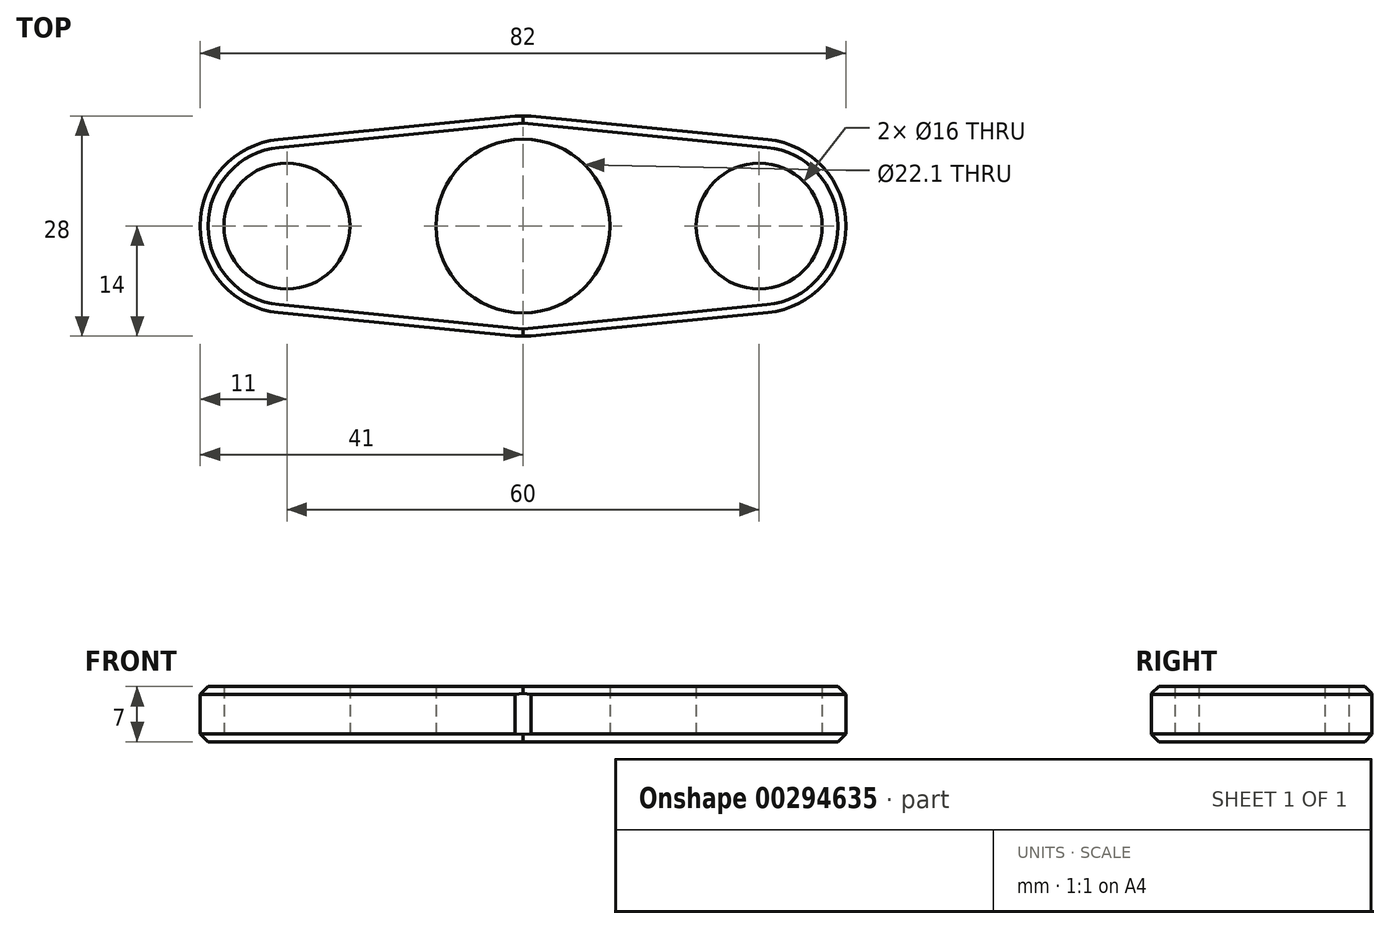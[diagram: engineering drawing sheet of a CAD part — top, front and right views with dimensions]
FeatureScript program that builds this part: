
annotation { "Feature Type Name" : "Feature", "Feature Type Description" : "" }
export const myFeature = defineFeature(function(context is Context, id is Id, definition is map)
    precondition{}
    {
        {
            var Q0;
            Q0=qCreatedBy(makeId("Top.planeOp"),FACE);
            var sketch = newSketch(context, id + "F0", { "sketchPlane" : qUnion([Q0])});
            skLineSegment(sketch, "E0.bottom", {"start": v(41, 14) * mm, "end": v(-41, 14) * mm});
            skLineSegment(sketch, "E0.top", {"start": v(41, -14) * mm, "end": v(-41, -14) * mm});
            skLineSegment(sketch, "E0.left", {"start": v(41, 14) * mm, "end": v(41, -14) * mm});
            skLineSegment(sketch, "E0.right", {"start": v(-41, 14) * mm, "end": v(-41, -14) * mm});
            skPoint(sketch, "E0.middle", {"position": v(0, 0) * mm});
            skCircle(sketch, "E1", {"center": v(0, 0) * mm, "radius": 11.05 * mm});
            skCircle(sketch, "E2", {"center": v(-30, 0) * mm, "radius": 8 * mm});
            skCircle(sketch, "E3", {"center": v(30, 0) * mm, "radius": 8 * mm});
            skSolve(sketch);
        }
        {
            var Q0;
            Q0=makeQuery(id+"F0.imprint","IMPRINT",FACE,{"disambiguationData":[TD([[makeQuery(id+"F0.imprint","IMPRINT",EDGE,{"derivedFrom":sQuery(id+"F0.wireOp",EDGE,"E0.bottom")}),1.0]])]});
            extrude(context, id + "F1", {"entities" : qUnion([Q0]), "depth" : 7 * mm});
        }
        {
            var Q0;
            Q0=makeQuery(id+"F1.opExtrude","SWEPT_EDGE",EDGE,{"disambiguationData":[OSD([sQuery(id+"F0.wireOp",EDGE,"E0.top"),sQuery(id+"F0.wireOp",EDGE,"E0.right")])]});
            var Q1;
            Q1=makeQuery(id+"F1.opExtrude","SWEPT_EDGE",EDGE,{"disambiguationData":[OSD([sQuery(id+"F0.wireOp",EDGE,"E0.top"),sQuery(id+"F0.wireOp",EDGE,"E0.left")])]});
            var Q2;
            Q2=makeQuery(id+"F1.opExtrude","SWEPT_EDGE",EDGE,{"disambiguationData":[OSD([sQuery(id+"F0.wireOp",EDGE,"E0.bottom"),sQuery(id+"F0.wireOp",EDGE,"E0.left")])]});
            var Q3;
            Q3=makeQuery(id+"F1.opExtrude","SWEPT_EDGE",EDGE,{"disambiguationData":[OSD([sQuery(id+"F0.wireOp",EDGE,"E0.bottom"),sQuery(id+"F0.wireOp",EDGE,"E0.right")])]});
            chamfer(context, id + "F2", {"entities" : qUnion([Q0, Q1, Q2, Q3]), "chamferType" : ChamferType.TWO_OFFSETS, "width1" : 40 * mm, "oppositeDirection" : false, "width2" : 4 * mm, "tangentPropagation" : true});
        }
        {
            var Q0;
            {var subQ0=sQuery(id+"F0.wireOp",EDGE,"E0.right");Q0=makeQuery(id+"F2.opChamfer","BLEND_EDGE",EDGE,{"blendedFrom":[makeQuery(id+"F1.opExtrude","SWEPT_EDGE",EDGE,{"disambiguationData":[OSD([sQuery(id+"F0.wireOp",EDGE,"E0.bottom"),subQ0])]}),makeQuery(id+"F1.opExtrude","SWEPT_FACE",FACE,{"disambiguationData":[OSD([subQ0])]})],"blendedInto":[makeQuery(id+"F1.opExtrude","SWEPT_FACE",FACE,{"disambiguationData":[OSD([subQ0])]})]});}
            var Q1;
            {var subQ0=sQuery(id+"F0.wireOp",EDGE,"E0.right");Q1=makeQuery(id+"F2.opChamfer","BLEND_EDGE",EDGE,{"blendedFrom":[makeQuery(id+"F1.opExtrude","SWEPT_EDGE",EDGE,{"disambiguationData":[OSD([sQuery(id+"F0.wireOp",EDGE,"E0.top"),subQ0])]}),makeQuery(id+"F1.opExtrude","SWEPT_FACE",FACE,{"disambiguationData":[OSD([subQ0])]})],"blendedInto":[makeQuery(id+"F1.opExtrude","SWEPT_FACE",FACE,{"disambiguationData":[OSD([subQ0])]})]});}
            var Q2;
            {var subQ0=sQuery(id+"F0.wireOp",EDGE,"E0.left");Q2=makeQuery(id+"F2.opChamfer","BLEND_EDGE",EDGE,{"blendedFrom":[makeQuery(id+"F1.opExtrude","SWEPT_EDGE",EDGE,{"disambiguationData":[OSD([sQuery(id+"F0.wireOp",EDGE,"E0.bottom"),subQ0])]}),makeQuery(id+"F1.opExtrude","SWEPT_FACE",FACE,{"disambiguationData":[OSD([subQ0])]})],"blendedInto":[makeQuery(id+"F1.opExtrude","SWEPT_FACE",FACE,{"disambiguationData":[OSD([subQ0])]})]});}
            var Q3;
            {var subQ0=sQuery(id+"F0.wireOp",EDGE,"E0.left");Q3=makeQuery(id+"F2.opChamfer","BLEND_EDGE",EDGE,{"blendedFrom":[makeQuery(id+"F1.opExtrude","SWEPT_EDGE",EDGE,{"disambiguationData":[OSD([sQuery(id+"F0.wireOp",EDGE,"E0.top"),subQ0])]}),makeQuery(id+"F1.opExtrude","SWEPT_FACE",FACE,{"disambiguationData":[OSD([subQ0])]})],"blendedInto":[makeQuery(id+"F1.opExtrude","SWEPT_FACE",FACE,{"disambiguationData":[OSD([subQ0])]})]});}
            fillet(context, id + "F3", {"entities" : qUnion([Q0, Q1, Q2, Q3]), "radius" : 11 * mm, "tangentPropagation" : true, "allowEdgeOverflow" : false});
        }
        {
            var Q0;
            {var subQ0=sQuery(id+"F0.wireOp",EDGE,"E0.right");var subQ1=sQuery(id+"F0.wireOp",EDGE,"E0.top");Q0=makeQuery(id+"F2.opChamfer","BLEND_EDGE",EDGE,{"blendedFrom":[makeQuery(id+"F1.opExtrude","SWEPT_EDGE",EDGE,{"disambiguationData":[OSD([subQ1,subQ0])]}),makeQuery(id+"F1.opExtrude","CAP_FACE",FACE,{"disambiguationData":[OSD([sQuery(id+"F0.wireOp",EDGE,"E0.bottom"),subQ1,sQuery(id+"F0.wireOp",EDGE,"E0.left"),subQ0,sQuery(id+"F0.wireOp",EDGE,"E1"),sQuery(id+"F0.wireOp",EDGE,"E2"),sQuery(id+"F0.wireOp",EDGE,"E3")])],"isStart":false})],"blendedInto":[makeQuery(id+"F1.opExtrude","CAP_FACE",FACE,{"disambiguationData":[OSD([sQuery(id+"F0.wireOp",EDGE,"E0.bottom"),subQ1,sQuery(id+"F0.wireOp",EDGE,"E0.left"),subQ0,sQuery(id+"F0.wireOp",EDGE,"E1"),sQuery(id+"F0.wireOp",EDGE,"E2"),sQuery(id+"F0.wireOp",EDGE,"E3")])],"isStart":false})]});}
            var Q1;
            {var subQ0=sQuery(id+"F0.wireOp",EDGE,"E0.left");var subQ1=sQuery(id+"F0.wireOp",EDGE,"E0.top");Q1=makeQuery(id+"F2.opChamfer","BLEND_EDGE",EDGE,{"blendedFrom":[makeQuery(id+"F1.opExtrude","SWEPT_EDGE",EDGE,{"disambiguationData":[OSD([subQ1,subQ0])]}),makeQuery(id+"F1.opExtrude","CAP_FACE",FACE,{"disambiguationData":[OSD([sQuery(id+"F0.wireOp",EDGE,"E0.bottom"),subQ1,subQ0,sQuery(id+"F0.wireOp",EDGE,"E0.right"),sQuery(id+"F0.wireOp",EDGE,"E1"),sQuery(id+"F0.wireOp",EDGE,"E2"),sQuery(id+"F0.wireOp",EDGE,"E3")])],"isStart":false})],"blendedInto":[makeQuery(id+"F1.opExtrude","CAP_FACE",FACE,{"disambiguationData":[OSD([sQuery(id+"F0.wireOp",EDGE,"E0.bottom"),subQ1,subQ0,sQuery(id+"F0.wireOp",EDGE,"E0.right"),sQuery(id+"F0.wireOp",EDGE,"E1"),sQuery(id+"F0.wireOp",EDGE,"E2"),sQuery(id+"F0.wireOp",EDGE,"E3")])],"isStart":false})]});}
            var Q2;
            {var subQ0=sQuery(id+"F0.wireOp",EDGE,"E0.left");var subQ1=sQuery(id+"F0.wireOp",EDGE,"E0.bottom");Q2=makeQuery(id+"F2.opChamfer","BLEND_EDGE",EDGE,{"blendedFrom":[makeQuery(id+"F1.opExtrude","SWEPT_EDGE",EDGE,{"disambiguationData":[OSD([subQ1,subQ0])]}),makeQuery(id+"F1.opExtrude","CAP_FACE",FACE,{"disambiguationData":[OSD([subQ1,sQuery(id+"F0.wireOp",EDGE,"E0.top"),subQ0,sQuery(id+"F0.wireOp",EDGE,"E0.right"),sQuery(id+"F0.wireOp",EDGE,"E1"),sQuery(id+"F0.wireOp",EDGE,"E2"),sQuery(id+"F0.wireOp",EDGE,"E3")])],"isStart":false})],"blendedInto":[makeQuery(id+"F1.opExtrude","CAP_FACE",FACE,{"disambiguationData":[OSD([subQ1,sQuery(id+"F0.wireOp",EDGE,"E0.top"),subQ0,sQuery(id+"F0.wireOp",EDGE,"E0.right"),sQuery(id+"F0.wireOp",EDGE,"E1"),sQuery(id+"F0.wireOp",EDGE,"E2"),sQuery(id+"F0.wireOp",EDGE,"E3")])],"isStart":false})]});}
            var Q3;
            {var subQ0=sQuery(id+"F0.wireOp",EDGE,"E0.right");var subQ1=sQuery(id+"F0.wireOp",EDGE,"E0.bottom");Q3=makeQuery(id+"F2.opChamfer","BLEND_EDGE",EDGE,{"blendedFrom":[makeQuery(id+"F1.opExtrude","SWEPT_EDGE",EDGE,{"disambiguationData":[OSD([subQ1,subQ0])]}),makeQuery(id+"F1.opExtrude","CAP_FACE",FACE,{"disambiguationData":[OSD([subQ1,sQuery(id+"F0.wireOp",EDGE,"E0.top"),sQuery(id+"F0.wireOp",EDGE,"E0.left"),subQ0,sQuery(id+"F0.wireOp",EDGE,"E1"),sQuery(id+"F0.wireOp",EDGE,"E2"),sQuery(id+"F0.wireOp",EDGE,"E3")])],"isStart":false})],"blendedInto":[makeQuery(id+"F1.opExtrude","CAP_FACE",FACE,{"disambiguationData":[OSD([subQ1,sQuery(id+"F0.wireOp",EDGE,"E0.top"),sQuery(id+"F0.wireOp",EDGE,"E0.left"),subQ0,sQuery(id+"F0.wireOp",EDGE,"E1"),sQuery(id+"F0.wireOp",EDGE,"E2"),sQuery(id+"F0.wireOp",EDGE,"E3")])],"isStart":false})]});}
            var Q4;
            {var subQ0=sQuery(id+"F0.wireOp",EDGE,"E0.left");var subQ1=sQuery(id+"F0.wireOp",EDGE,"E0.top");Q4=makeQuery(id+"F2.opChamfer","BLEND_EDGE",EDGE,{"blendedFrom":[makeQuery(id+"F1.opExtrude","SWEPT_EDGE",EDGE,{"disambiguationData":[OSD([subQ1,subQ0])]}),makeQuery(id+"F1.opExtrude","CAP_FACE",FACE,{"disambiguationData":[OSD([sQuery(id+"F0.wireOp",EDGE,"E0.bottom"),subQ1,subQ0,sQuery(id+"F0.wireOp",EDGE,"E0.right"),sQuery(id+"F0.wireOp",EDGE,"E1"),sQuery(id+"F0.wireOp",EDGE,"E2"),sQuery(id+"F0.wireOp",EDGE,"E3")])],"isStart":true})],"blendedInto":[makeQuery(id+"F1.opExtrude","CAP_FACE",FACE,{"disambiguationData":[OSD([sQuery(id+"F0.wireOp",EDGE,"E0.bottom"),subQ1,subQ0,sQuery(id+"F0.wireOp",EDGE,"E0.right"),sQuery(id+"F0.wireOp",EDGE,"E1"),sQuery(id+"F0.wireOp",EDGE,"E2"),sQuery(id+"F0.wireOp",EDGE,"E3")])],"isStart":true})]});}
            var Q5;
            {var subQ0=sQuery(id+"F0.wireOp",EDGE,"E0.right");var subQ1=sQuery(id+"F0.wireOp",EDGE,"E0.top");Q5=makeQuery(id+"F2.opChamfer","BLEND_EDGE",EDGE,{"blendedFrom":[makeQuery(id+"F1.opExtrude","SWEPT_EDGE",EDGE,{"disambiguationData":[OSD([subQ1,subQ0])]}),makeQuery(id+"F1.opExtrude","CAP_FACE",FACE,{"disambiguationData":[OSD([sQuery(id+"F0.wireOp",EDGE,"E0.bottom"),subQ1,sQuery(id+"F0.wireOp",EDGE,"E0.left"),subQ0,sQuery(id+"F0.wireOp",EDGE,"E1"),sQuery(id+"F0.wireOp",EDGE,"E2"),sQuery(id+"F0.wireOp",EDGE,"E3")])],"isStart":true})],"blendedInto":[makeQuery(id+"F1.opExtrude","CAP_FACE",FACE,{"disambiguationData":[OSD([sQuery(id+"F0.wireOp",EDGE,"E0.bottom"),subQ1,sQuery(id+"F0.wireOp",EDGE,"E0.left"),subQ0,sQuery(id+"F0.wireOp",EDGE,"E1"),sQuery(id+"F0.wireOp",EDGE,"E2"),sQuery(id+"F0.wireOp",EDGE,"E3")])],"isStart":true})]});}
            var Q6;
            {var subQ0=sQuery(id+"F0.wireOp",EDGE,"E0.left");var subQ1=sQuery(id+"F0.wireOp",EDGE,"E0.bottom");Q6=makeQuery(id+"F2.opChamfer","BLEND_EDGE",EDGE,{"blendedFrom":[makeQuery(id+"F1.opExtrude","SWEPT_EDGE",EDGE,{"disambiguationData":[OSD([subQ1,subQ0])]}),makeQuery(id+"F1.opExtrude","CAP_FACE",FACE,{"disambiguationData":[OSD([subQ1,sQuery(id+"F0.wireOp",EDGE,"E0.top"),subQ0,sQuery(id+"F0.wireOp",EDGE,"E0.right"),sQuery(id+"F0.wireOp",EDGE,"E1"),sQuery(id+"F0.wireOp",EDGE,"E2"),sQuery(id+"F0.wireOp",EDGE,"E3")])],"isStart":true})],"blendedInto":[makeQuery(id+"F1.opExtrude","CAP_FACE",FACE,{"disambiguationData":[OSD([subQ1,sQuery(id+"F0.wireOp",EDGE,"E0.top"),subQ0,sQuery(id+"F0.wireOp",EDGE,"E0.right"),sQuery(id+"F0.wireOp",EDGE,"E1"),sQuery(id+"F0.wireOp",EDGE,"E2"),sQuery(id+"F0.wireOp",EDGE,"E3")])],"isStart":true})]});}
            var Q7;
            {var subQ0=sQuery(id+"F0.wireOp",EDGE,"E0.right");var subQ1=sQuery(id+"F0.wireOp",EDGE,"E0.bottom");Q7=makeQuery(id+"F2.opChamfer","BLEND_EDGE",EDGE,{"blendedFrom":[makeQuery(id+"F1.opExtrude","SWEPT_EDGE",EDGE,{"disambiguationData":[OSD([subQ1,subQ0])]}),makeQuery(id+"F1.opExtrude","CAP_FACE",FACE,{"disambiguationData":[OSD([subQ1,sQuery(id+"F0.wireOp",EDGE,"E0.top"),sQuery(id+"F0.wireOp",EDGE,"E0.left"),subQ0,sQuery(id+"F0.wireOp",EDGE,"E1"),sQuery(id+"F0.wireOp",EDGE,"E2"),sQuery(id+"F0.wireOp",EDGE,"E3")])],"isStart":true})],"blendedInto":[makeQuery(id+"F1.opExtrude","CAP_FACE",FACE,{"disambiguationData":[OSD([subQ1,sQuery(id+"F0.wireOp",EDGE,"E0.top"),sQuery(id+"F0.wireOp",EDGE,"E0.left"),subQ0,sQuery(id+"F0.wireOp",EDGE,"E1"),sQuery(id+"F0.wireOp",EDGE,"E2"),sQuery(id+"F0.wireOp",EDGE,"E3")])],"isStart":true})]});}
            chamfer(context, id + "F4", {"entities" : qUnion([Q0, Q1, Q2, Q3, Q4, Q5, Q6, Q7]), "width" : 1 * mm, "tangentPropagation" : true});
        }
    });
